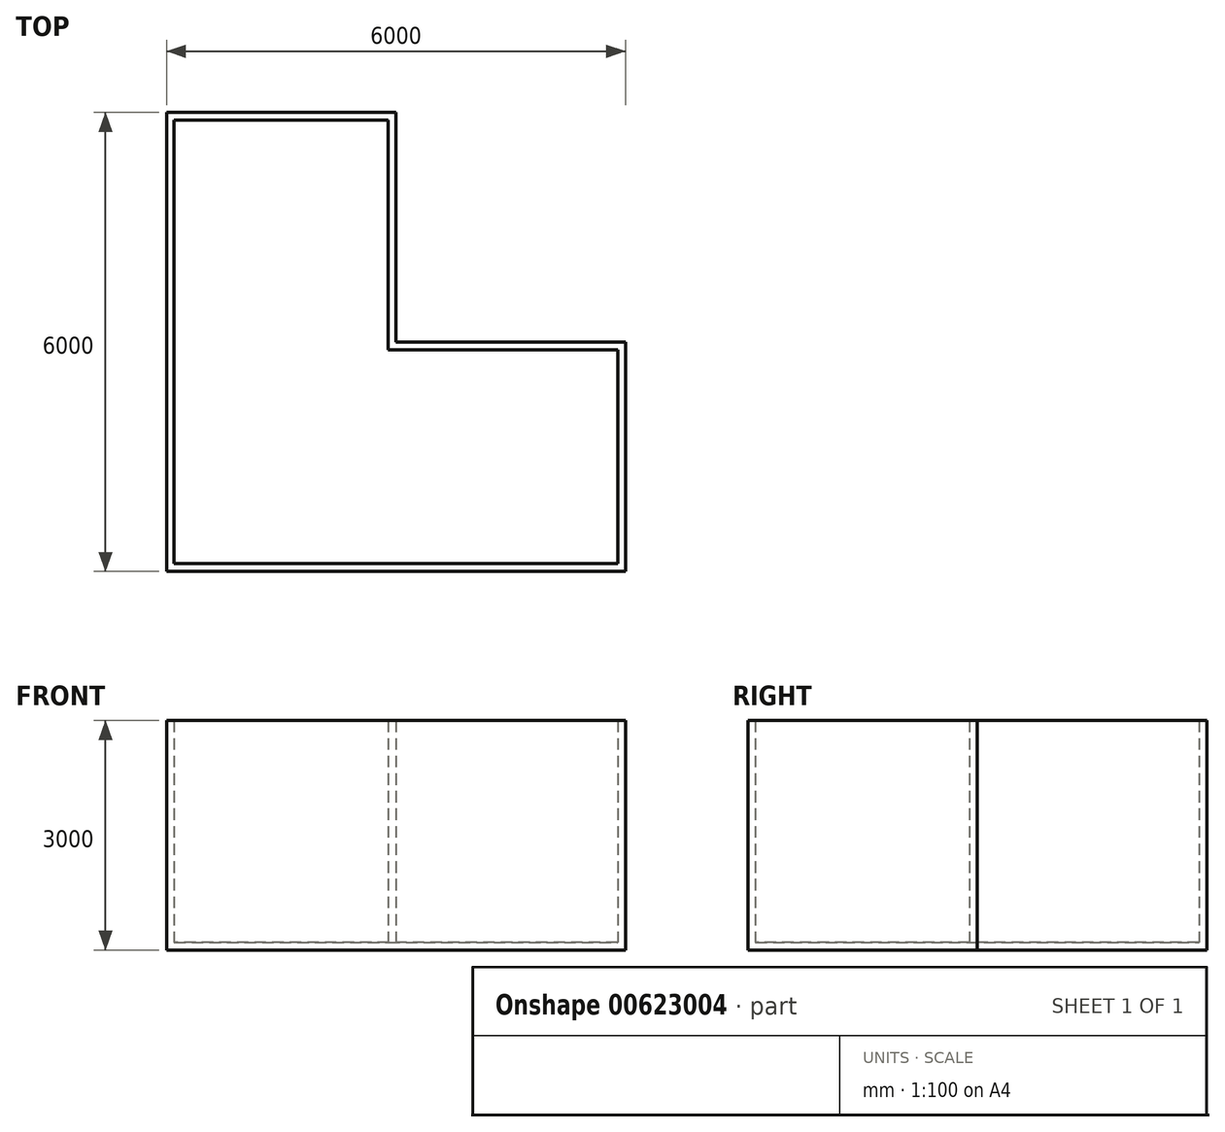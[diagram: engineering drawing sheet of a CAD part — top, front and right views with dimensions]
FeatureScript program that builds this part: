
annotation { "Feature Type Name" : "Feature", "Feature Type Description" : "" }
export const myFeature = defineFeature(function(context is Context, id is Id, definition is map)
    precondition{}
    {
        {
            var Q0;
            Q0=qCreatedBy(makeId("Top.planeOp"),FACE);
            var sketch = newSketch(context, id + "F0", { "sketchPlane" : qUnion([Q0])});
            skLineSegment(sketch, "E0", {"start": v(0, 0) * mm, "end": v(-6000, 0) * mm});
            skLineSegment(sketch, "E1", {"start": v(-6000, 0) * mm, "end": v(-6000, 6000) * mm});
            skLineSegment(sketch, "E2", {"start": v(-6000, 6000) * mm, "end": v(-3000, 6000) * mm});
            skLineSegment(sketch, "E3", {"start": v(-3000, 6000) * mm, "end": v(-3000, 3000) * mm});
            skLineSegment(sketch, "E4", {"start": v(-3000, 3000) * mm, "end": v(0, 3000) * mm});
            skLineSegment(sketch, "E5", {"start": v(0, 3000) * mm, "end": v(0, 0) * mm});
            skSolve(sketch);
        }
        {
            var Q0;
            Q0 = qSketchRegion(id + "F0", true);
            extrude(context, id + "F1", {"entities" : qUnion([Q0]), "depth" : 3000 * mm, "offsetDistance" : 25 * mm});
        }
        {
            var Q0;
            Q0=makeQuery(id+"F1.opExtrude","CAP_FACE",FACE,{"disambiguationData":[OSD([sQuery(id+"F0.wireOp",EDGE,"E0"),sQuery(id+"F0.wireOp",EDGE,"E1"),sQuery(id+"F0.wireOp",EDGE,"E2"),sQuery(id+"F0.wireOp",EDGE,"E3"),sQuery(id+"F0.wireOp",EDGE,"E4"),sQuery(id+"F0.wireOp",EDGE,"E5")])],"isStart":false});
            shell(context, id + "F2", {"entities" : qUnion([Q0]), "thickness" : 100 * mm});
        }
    });
